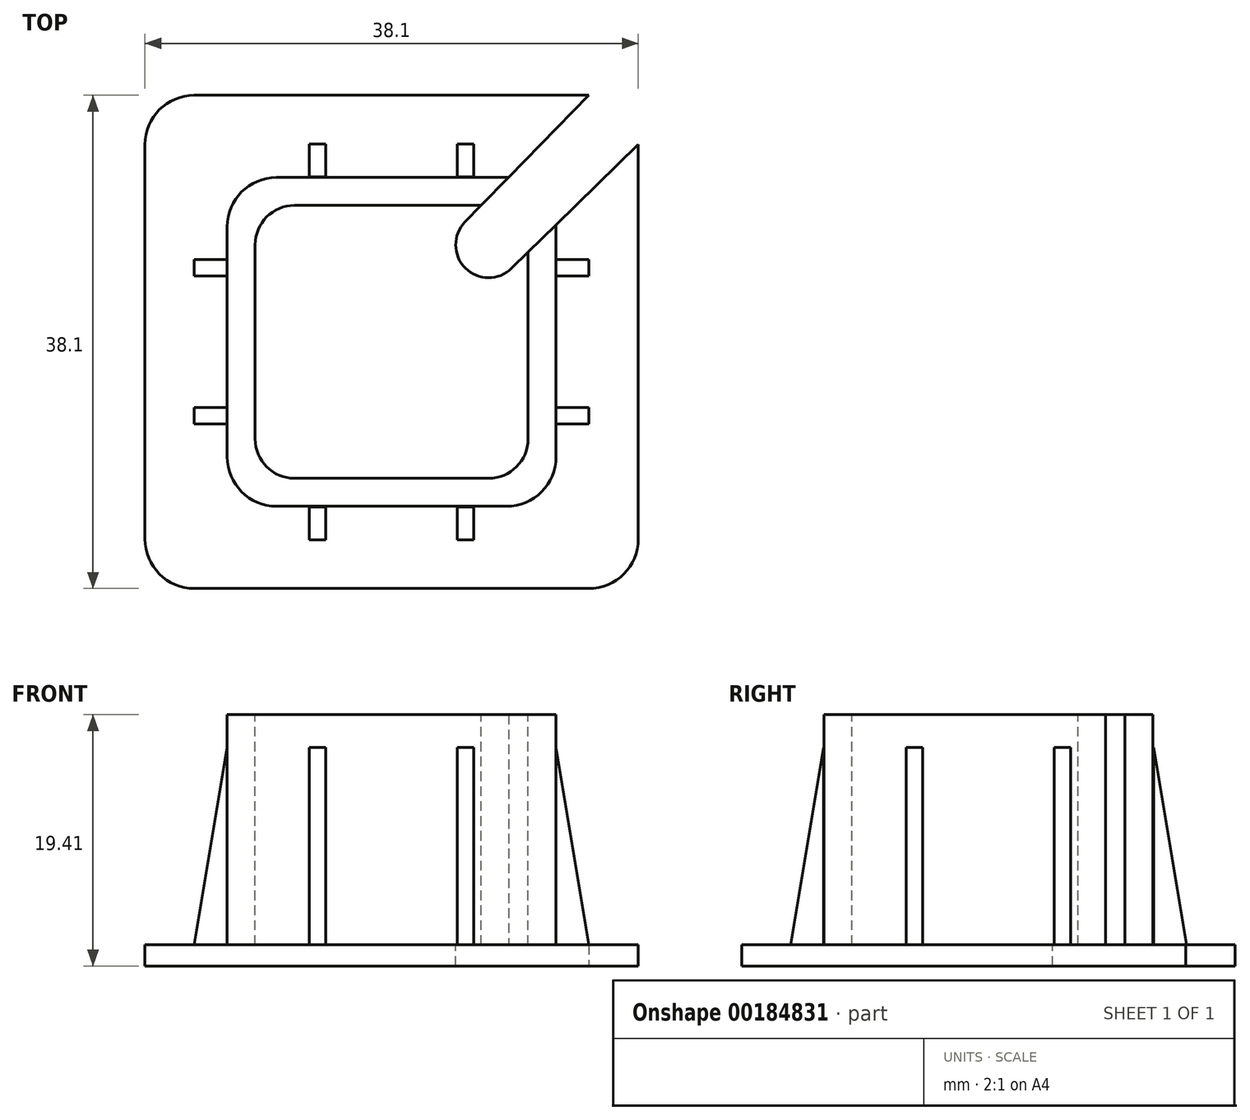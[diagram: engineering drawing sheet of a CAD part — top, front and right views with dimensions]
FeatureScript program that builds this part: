
annotation { "Feature Type Name" : "Feature", "Feature Type Description" : "" }
export const myFeature = defineFeature(function(context is Context, id is Id, definition is map)
    precondition{}
    {
        {
            var Q0;
            Q0=qCreatedBy(makeId("Top.planeOp"),FACE);
            var sketch = newSketch(context, id + "F0", { "sketchPlane" : qUnion([Q0])});
            skLineSegment(sketch, "E0.bottom", {"start": v(15.24, -19.05) * mm, "end": v(-15.24, -19.05) * mm});
            skLineSegment(sketch, "E0.top", {"start": v(15.24, 19.05) * mm, "end": v(-15.24, 19.05) * mm});
            skLineSegment(sketch, "E0.left", {"start": v(19.05, -15.24) * mm, "end": v(19.05, 15.24) * mm});
            skLineSegment(sketch, "E0.right", {"start": v(-19.05, -15.24) * mm, "end": v(-19.05, 15.24) * mm});
            skPoint(sketch, "E0.middle", {"position": v(0, 0) * mm});
            skPoint(sketch, "E1.visualSharp", {"position": v(-19.05, 19.05) * mm});
            skArc(sketch, "E1.filletArc", {"start": v(-15.24, 19.05) * mm, "mid": v(-17.93, 17.93) * mm, "end": v(-19.05, 15.24) * mm});
            skPoint(sketch, "E2.visualSharp", {"position": v(19.05, 19.05) * mm});
            skArc(sketch, "E2.filletArc", {"start": v(19.05, 15.24) * mm, "mid": v(17.93, 17.93) * mm, "end": v(15.24, 19.05) * mm});
            skPoint(sketch, "E3.visualSharp", {"position": v(19.05, -19.05) * mm});
            skArc(sketch, "E3.filletArc", {"start": v(15.24, -19.05) * mm, "mid": v(17.93, -17.93) * mm, "end": v(19.05, -15.24) * mm});
            skPoint(sketch, "E4.visualSharp", {"position": v(-19.05, -19.05) * mm});
            skArc(sketch, "E4.filletArc", {"start": v(-19.05, -15.24) * mm, "mid": v(-17.93, -17.93) * mm, "end": v(-15.24, -19.05) * mm});
            skSolve(sketch);
        }
        {
            var Q0;
            Q0 = qSketchRegion(id + "F0", true);
            extrude(context, id + "F1", {"entities" : qUnion([Q0]), "depth" : 1.63 * mm});
        }
        {
            var Q0;
            Q0=makeQuery(id+"F1.opExtrude","CAP_FACE",FACE,{"disambiguationData":[OSD([sQuery(id+"F0.wireOp",EDGE,"E0.bottom"),sQuery(id+"F0.wireOp",EDGE,"E0.top"),sQuery(id+"F0.wireOp",EDGE,"E0.left"),sQuery(id+"F0.wireOp",EDGE,"E0.right"),sQuery(id+"F0.wireOp",EDGE,"E1.filletArc"),sQuery(id+"F0.wireOp",EDGE,"E2.filletArc"),sQuery(id+"F0.wireOp",EDGE,"E3.filletArc"),sQuery(id+"F0.wireOp",EDGE,"E4.filletArc")])],"isStart":false});
            var sketch = newSketch(context, id + "F2", { "sketchPlane" : qUnion([Q0])});
            skLineSegment(sketch, "E5.bottom", {"start": v(8.89, -12.7) * mm, "end": v(-8.9, -12.7) * mm});
            skLineSegment(sketch, "E5.top", {"start": v(8.89, 12.7) * mm, "end": v(-8.9, 12.7) * mm});
            skLineSegment(sketch, "E5.left", {"start": v(12.7, -8.9) * mm, "end": v(12.7, 8.9) * mm});
            skLineSegment(sketch, "E5.right", {"start": v(-12.7, -8.9) * mm, "end": v(-12.7, 8.9) * mm});
            skPoint(sketch, "E5.middle", {"position": v(0, 0) * mm});
            skPoint(sketch, "E6.visualSharp", {"position": v(-12.7, 12.7) * mm});
            skArc(sketch, "E6.filletArc", {"start": v(-8.9, 12.7) * mm, "mid": v(-11.58, 11.58) * mm, "end": v(-12.7, 8.9) * mm});
            skPoint(sketch, "E7.visualSharp", {"position": v(12.7, 12.7) * mm});
            skArc(sketch, "E7.filletArc", {"start": v(12.7, 8.9) * mm, "mid": v(11.58, 11.58) * mm, "end": v(8.89, 12.7) * mm});
            skPoint(sketch, "E8.visualSharp", {"position": v(12.7, -12.7) * mm});
            skArc(sketch, "E8.filletArc", {"start": v(8.9, -12.7) * mm, "mid": v(11.58, -11.58) * mm, "end": v(12.7, -8.9) * mm});
            skPoint(sketch, "E9.visualSharp", {"position": v(-12.7, -12.7) * mm});
            skArc(sketch, "E9.filletArc", {"start": v(-12.7, -8.9) * mm, "mid": v(-11.58, -11.58) * mm, "end": v(-8.9, -12.7) * mm});
            skSolve(sketch);
        }
        {
            var Q0;
            Q0 = qSketchRegion(id + "F2", true);
            extrude(context, id + "F3", {"entities" : qUnion([Q0]), "operationType" : NewBodyOperationType.ADD, "depth" : 17.78 * mm});
        }
        {
            var Q0;
            Q0=makeQuery(id+"F3.opExtrude","CAP_FACE",FACE,{"disambiguationData":[OSD([sQuery(id+"F2.wireOp",EDGE,"E5.bottom"),sQuery(id+"F2.wireOp",EDGE,"E5.top"),sQuery(id+"F2.wireOp",EDGE,"E5.left"),sQuery(id+"F2.wireOp",EDGE,"E5.right"),sQuery(id+"F2.wireOp",EDGE,"E6.filletArc"),sQuery(id+"F2.wireOp",EDGE,"E7.filletArc"),sQuery(id+"F2.wireOp",EDGE,"E8.filletArc"),sQuery(id+"F2.wireOp",EDGE,"E9.filletArc")])],"isStart":false});
            var sketch = newSketch(context, id + "F4", { "sketchPlane" : qUnion([Q0])});
            skLineSegment(sketch, "E10.0", {"start": v(-7.5, -10.54) * mm, "end": v(7.5, -10.54) * mm});
            skLineSegment(sketch, "E10.1", {"start": v(-10.54, 7.5) * mm, "end": v(-10.54, -7.5) * mm});
            skLineSegment(sketch, "E10.2", {"start": v(7.5, 10.54) * mm, "end": v(-7.5, 10.54) * mm});
            skLineSegment(sketch, "E10.3", {"start": v(10.54, -7.5) * mm, "end": v(10.54, 7.5) * mm});
            skPoint(sketch, "E11.visualSharp", {"position": v(-10.54, 10.54) * mm});
            skArc(sketch, "E11.filletArc", {"start": v(-7.5, 10.54) * mm, "mid": v(-9.65, 9.65) * mm, "end": v(-10.54, 7.5) * mm});
            skPoint(sketch, "E12.visualSharp", {"position": v(10.54, 10.54) * mm});
            skArc(sketch, "E12.filletArc", {"start": v(10.54, 7.5) * mm, "mid": v(9.65, 9.65) * mm, "end": v(7.5, 10.54) * mm});
            skPoint(sketch, "E13.visualSharp", {"position": v(10.54, -10.54) * mm});
            skArc(sketch, "E13.filletArc", {"start": v(7.5, -10.54) * mm, "mid": v(9.65, -9.65) * mm, "end": v(10.54, -7.5) * mm});
            skPoint(sketch, "E14.visualSharp", {"position": v(-10.54, -10.54) * mm});
            skArc(sketch, "E14.filletArc", {"start": v(-10.54, -7.5) * mm, "mid": v(-9.65, -9.65) * mm, "end": v(-7.5, -10.54) * mm});
            skSolve(sketch);
        }
        {
            var Q0;
            Q0 = qSketchRegion(id + "F4", true);
            var Q1;
            Q1=makeQuery(id+"F1.opExtrude","CAP_FACE",FACE,{"disambiguationData":[OSD([sQuery(id+"F0.wireOp",EDGE,"E0.bottom"),sQuery(id+"F0.wireOp",EDGE,"E0.top"),sQuery(id+"F0.wireOp",EDGE,"E0.left"),sQuery(id+"F0.wireOp",EDGE,"E0.right"),sQuery(id+"F0.wireOp",EDGE,"E1.filletArc"),sQuery(id+"F0.wireOp",EDGE,"E2.filletArc"),sQuery(id+"F0.wireOp",EDGE,"E3.filletArc"),sQuery(id+"F0.wireOp",EDGE,"E4.filletArc")])],"isStart":false});
            extrude(context, id + "F5", {"entities" : qUnion([Q0]), "operationType" : NewBodyOperationType.REMOVE, "endBound" : BoundingType.UP_TO_SURFACE, "oppositeDirection" : true, "endBoundEntityFace" : qUnion([Q1]), "depth" : 25.4 * mm});
        }
        {
            var Q0;
            Q0=makeQuery(id+"F1.opExtrude","CAP_FACE",FACE,{"disambiguationData":[OSD([sQuery(id+"F0.wireOp",EDGE,"E0.bottom"),sQuery(id+"F0.wireOp",EDGE,"E0.top"),sQuery(id+"F0.wireOp",EDGE,"E0.left"),sQuery(id+"F0.wireOp",EDGE,"E0.right"),sQuery(id+"F0.wireOp",EDGE,"E1.filletArc"),sQuery(id+"F0.wireOp",EDGE,"E2.filletArc"),sQuery(id+"F0.wireOp",EDGE,"E3.filletArc"),sQuery(id+"F0.wireOp",EDGE,"E4.filletArc")])],"isStart":false});
            var sketch = newSketch(context, id + "F6", { "sketchPlane" : qUnion([Q0])});
            skLineSegment(sketch, "E15.bottom", {"start": v(12.7, 6.35) * mm, "end": v(15.24, 6.35) * mm});
            skLineSegment(sketch, "E15.top", {"start": v(12.7, 5.08) * mm, "end": v(15.24, 5.08) * mm});
            skLineSegment(sketch, "E15.left", {"start": v(12.7, 6.35) * mm, "end": v(12.7, 5.08) * mm});
            skLineSegment(sketch, "E15.right", {"start": v(15.24, 6.35) * mm, "end": v(15.24, 5.08) * mm});
            skLineSegment(sketch, "E16.MirrorCS", {"start": v(-12.7, 6.35) * mm, "end": v(-15.24, 6.35) * mm});
            skLineSegment(sketch, "E17.MirrorCS", {"start": v(-12.7, 5.08) * mm, "end": v(-15.24, 5.08) * mm});
            skLineSegment(sketch, "E18.MirrorCS", {"start": v(-12.7, 6.35) * mm, "end": v(-12.7, 5.08) * mm});
            skLineSegment(sketch, "E19.MirrorCS", {"start": v(-15.24, 6.35) * mm, "end": v(-15.24, 5.08) * mm});
            skLineSegment(sketch, "E20.MirrorCS", {"start": v(-15.24, -6.35) * mm, "end": v(-15.24, -5.08) * mm});
            skLineSegment(sketch, "E21.MirrorCS", {"start": v(-12.7, -6.35) * mm, "end": v(-12.7, -5.08) * mm});
            skLineSegment(sketch, "E22.MirrorCS", {"start": v(-12.7, -5.08) * mm, "end": v(-15.24, -5.08) * mm});
            skLineSegment(sketch, "E23.MirrorCS", {"start": v(-12.7, -6.35) * mm, "end": v(-15.24, -6.35) * mm});
            skLineSegment(sketch, "E24.MirrorCS", {"start": v(15.24, -6.35) * mm, "end": v(15.24, -5.08) * mm});
            skLineSegment(sketch, "E25.MirrorCS", {"start": v(12.7, -6.35) * mm, "end": v(12.7, -5.08) * mm});
            skLineSegment(sketch, "E26.MirrorCS", {"start": v(12.7, -5.08) * mm, "end": v(15.24, -5.08) * mm});
            skLineSegment(sketch, "E27.MirrorCS", {"start": v(12.7, -6.35) * mm, "end": v(15.24, -6.35) * mm});
            skLineSegment(sketch, "E28.bottom", {"start": v(5.08, 12.75) * mm, "end": v(6.35, 12.75) * mm});
            skLineSegment(sketch, "E28.top", {"start": v(5.08, 15.29) * mm, "end": v(6.35, 15.29) * mm});
            skLineSegment(sketch, "E28.left", {"start": v(5.08, 12.75) * mm, "end": v(5.08, 15.29) * mm});
            skLineSegment(sketch, "E28.right", {"start": v(6.35, 12.75) * mm, "end": v(6.35, 15.29) * mm});
            skLineSegment(sketch, "E29.MirrorCS", {"start": v(-6.35, 12.75) * mm, "end": v(-6.35, 15.29) * mm});
            skLineSegment(sketch, "E30.MirrorCS", {"start": v(-5.08, 15.29) * mm, "end": v(-6.35, 15.29) * mm});
            skLineSegment(sketch, "E31.MirrorCS", {"start": v(-5.08, 12.75) * mm, "end": v(-6.35, 12.75) * mm});
            skLineSegment(sketch, "E32.MirrorCS", {"start": v(-5.08, 12.75) * mm, "end": v(-5.08, 15.29) * mm});
            skLineSegment(sketch, "E33.MirrorCS", {"start": v(5.08, -12.75) * mm, "end": v(6.35, -12.75) * mm});
            skLineSegment(sketch, "E34.MirrorCS", {"start": v(-5.08, -12.75) * mm, "end": v(-6.35, -12.75) * mm});
            skLineSegment(sketch, "E35.MirrorCS", {"start": v(5.08, -15.29) * mm, "end": v(6.35, -15.29) * mm});
            skLineSegment(sketch, "E36.MirrorCS", {"start": v(-5.08, -15.29) * mm, "end": v(-6.35, -15.29) * mm});
            skLineSegment(sketch, "E37.MirrorCS", {"start": v(-6.35, -12.75) * mm, "end": v(-6.35, -15.29) * mm});
            skLineSegment(sketch, "E38.MirrorCS", {"start": v(5.08, -12.75) * mm, "end": v(5.08, -15.29) * mm});
            skLineSegment(sketch, "E39.MirrorCS", {"start": v(-5.08, -12.75) * mm, "end": v(-5.08, -15.29) * mm});
            skLineSegment(sketch, "E40.MirrorCS", {"start": v(6.35, -12.75) * mm, "end": v(6.35, -15.29) * mm});
            skSolve(sketch);
        }
        {
            var Q0;
            Q0 = qSketchRegion(id + "F6", true);
            extrude(context, id + "F7", {"entities" : qUnion([Q0]), "operationType" : NewBodyOperationType.ADD, "depth" : 15.24 * mm});
        }
        {
            var Q0;
            Q0=makeQuery(id+"F7.opExtrude","SWEPT_FACE",FACE,{"disambiguationData":[OSD([sQuery(id+"F6.wireOp",EDGE,"E27.MirrorCS")])]});
            var sketch = newSketch(context, id + "F8", { "sketchPlane" : qUnion([Q0])});
            skLineSegment(sketch, "E41.0", {"start": v(12.7, 16.87) * mm, "end": v(15.24, 16.87) * mm});
            skLineSegment(sketch, "E42.0", {"start": v(15.24, 16.87) * mm, "end": v(15.24, 1.63) * mm});
            skLineSegment(sketch, "E43", {"start": v(12.7, 16.87) * mm, "end": v(15.24, 1.63) * mm});
            skLineSegment(sketch, "E44.MirrorCS", {"start": v(-12.7, 16.87) * mm, "end": v(-15.24, 16.87) * mm});
            skLineSegment(sketch, "E45.MirrorCS", {"start": v(-12.7, 16.87) * mm, "end": v(-15.24, 1.63) * mm});
            skLineSegment(sketch, "E46.MirrorCS", {"start": v(-15.24, 16.87) * mm, "end": v(-15.24, 1.63) * mm});
            skSolve(sketch);
        }
        {
            var Q0;
            Q0 = qSketchRegion(id + "F8", true);
            extrude(context, id + "F9", {"entities" : qUnion([Q0]), "operationType" : NewBodyOperationType.REMOVE, "endBound" : BoundingType.THROUGH_ALL, "oppositeDirection" : true, "depth" : 25.4 * mm});
        }
        {
            var Q0;
            Q0=makeQuery(id+"F7.opExtrude","SWEPT_FACE",FACE,{"disambiguationData":[OSD([sQuery(id+"F6.wireOp",EDGE,"E28.right")])]});
            var sketch = newSketch(context, id + "F10", { "sketchPlane" : qUnion([Q0])});
            skLineSegment(sketch, "E47.0", {"start": v(12.75, 16.87) * mm, "end": v(15.29, 16.87) * mm});
            skLineSegment(sketch, "E48.0", {"start": v(15.29, 16.87) * mm, "end": v(15.29, 1.63) * mm});
            skLineSegment(sketch, "E49", {"start": v(12.75, 16.87) * mm, "end": v(15.29, 1.63) * mm});
            skLineSegment(sketch, "E50.MirrorCS", {"start": v(-12.75, 16.87) * mm, "end": v(-15.29, 1.63) * mm});
            skLineSegment(sketch, "E51.MirrorCS", {"start": v(-12.75, 16.87) * mm, "end": v(-15.29, 16.87) * mm});
            skLineSegment(sketch, "E52.MirrorCS", {"start": v(-15.29, 16.87) * mm, "end": v(-15.29, 1.63) * mm});
            skSolve(sketch);
        }
        {
            var Q0;
            Q0 = qSketchRegion(id + "F10", true);
            extrude(context, id + "F11", {"entities" : qUnion([Q0]), "operationType" : NewBodyOperationType.REMOVE, "endBound" : BoundingType.THROUGH_ALL, "oppositeDirection" : true, "depth" : 25.4 * mm});
        }
        {
            var Q0;
            Q0=makeQuery(id+"F5.boolean.opBoolean","COPY",FACE,{"derivedFrom":makeQuery(id+"F5.opExtrude","CAP_FACE",FACE,{"disambiguationData":[OSD([sQuery(id+"F4.wireOp",EDGE,"E10.0"),sQuery(id+"F4.wireOp",EDGE,"E10.1"),sQuery(id+"F4.wireOp",EDGE,"E10.2"),sQuery(id+"F4.wireOp",EDGE,"E10.3"),sQuery(id+"F4.wireOp",EDGE,"E11.filletArc"),sQuery(id+"F4.wireOp",EDGE,"E12.filletArc"),sQuery(id+"F4.wireOp",EDGE,"E13.filletArc"),sQuery(id+"F4.wireOp",EDGE,"E14.filletArc")])],"isStart":false})});
            var sketch = newSketch(context, id + "F12", { "sketchPlane" : qUnion([Q0])});
            skArc(sketch, "E53", {"start": v(5.68, 9.27) * mm, "mid": v(5.7, 5.7) * mm, "end": v(9.27, 5.68) * mm});
            skArc(sketch, "E54.0", {"start": v(19.05, 15.24) * mm, "mid": v(17.93, 17.93) * mm, "end": v(15.24, 19.05) * mm});
            skLineSegment(sketch, "E55", {"start": v(15.24, 19.05) * mm, "end": v(5.68, 9.27) * mm});
            skLineSegment(sketch, "E56", {"start": v(19.05, 15.24) * mm, "end": v(9.27, 5.68) * mm});
            skSolve(sketch);
        }
        {
            var Q0;
            Q0 = qSketchRegion(id + "F12", true);
            extrude(context, id + "F13", {"entities" : qUnion([Q0]), "operationType" : NewBodyOperationType.REMOVE, "endBound" : BoundingType.THROUGH_ALL, "oppositeDirection" : true, "depth" : 25.4 * mm, "hasSecondDirection" : true, "secondDirectionBound" : SecondDirectionBoundingType.THROUGH_ALL, "secondDirectionOppositeDirection" : false, "secondDirectionDepth" : 25.4 * mm});
        }
    });
